# Revit family: Sound Silencer - Ceiling and Wall Panels - Bevel
name_source: partatom
category: Specialty Equipment
units: mm (PartAtom-declared; Revit-internal decimal feet)

## family parameters
Always vertical = No
Cut with Voids When Loaded = No
Enable Cutting in Views = Yes
Maintain Annotation Orientation = No
OmniClass Number = 23.35.00.00
OmniClass Title = Covering, Cladding, and Finishes
Part Type = Normal
Room Calculation Point = No
Round Connector Dimension = Use Diameter
Shared = No
Work Plane-Based = Yes

## types (8) — shared parameters
Acoustics - NRC = Sound absorption varies from NRC 0.45 to 0.95 based on installation method used when tested per ASTM C423.
Assembly Code = C30
Default Elevation = 4' - 0"
Description = Acoustical Panels
Fire Rating = ASTM E84 - Class A
Manufacturer = Acoustical Surfaces, Inc.
Material = Sound Silencer
Model = Sound Silence Acoustical Panels
Recycled Content Percentage = 0%
Type Comments = Acoustical Panels
URL = https://www.acousticalsurfaces.com
Width = 2' - 0"

## per-type parameters (varying)
| type | A | Finish | Length | Thickness |
| 2 INCH - 24x48 - Charcoal | 0' - 1" | Paint - Acoustical-Surfaces - Sound Silencer - Charcoal | 4' - 0" | 0' - 2" |
| 2 INCH - 24x48 - White | 0' - 1" | Paint - Acoustical-Surfaces - Sound Silencer - White | 4' - 0" | 0' - 2" |
| 1 INCH - 24x48 - Charcoal | 0' - 0 1/2" | Paint - Acoustical-Surfaces - Sound Silencer - Charcoal | 4' - 0" | 0' - 1" |
| 1 INCH - 24x48 - White | 0' - 0 1/2" | Paint - Acoustical-Surfaces - Sound Silencer - White | 4' - 0" | 0' - 1" |
| 1 INCH - 24x24 - Charcoal | 0' - 0 1/2" | Paint - Acoustical-Surfaces - Sound Silencer - Charcoal | 2' - 0" | 0' - 1" |
| 2 INCH - 24x24 - Charcoal | 0' - 1" | Paint - Acoustical-Surfaces - Sound Silencer - Charcoal | 2' - 0" | 0' - 2" |
| 2 INCH - 24x24 - White | 0' - 1" | Paint - Acoustical-Surfaces - Sound Silencer - White | 2' - 0" | 0' - 2" |
| 1 INCH - 24x24 - White | 0' - 0 1/2" | Paint - Acoustical-Surfaces - Sound Silencer - White | 2' - 0" | 0' - 1" |

## geometry (parser evidence)
native form markers: Sweep x5
no freeform markers — native parametric forms only
